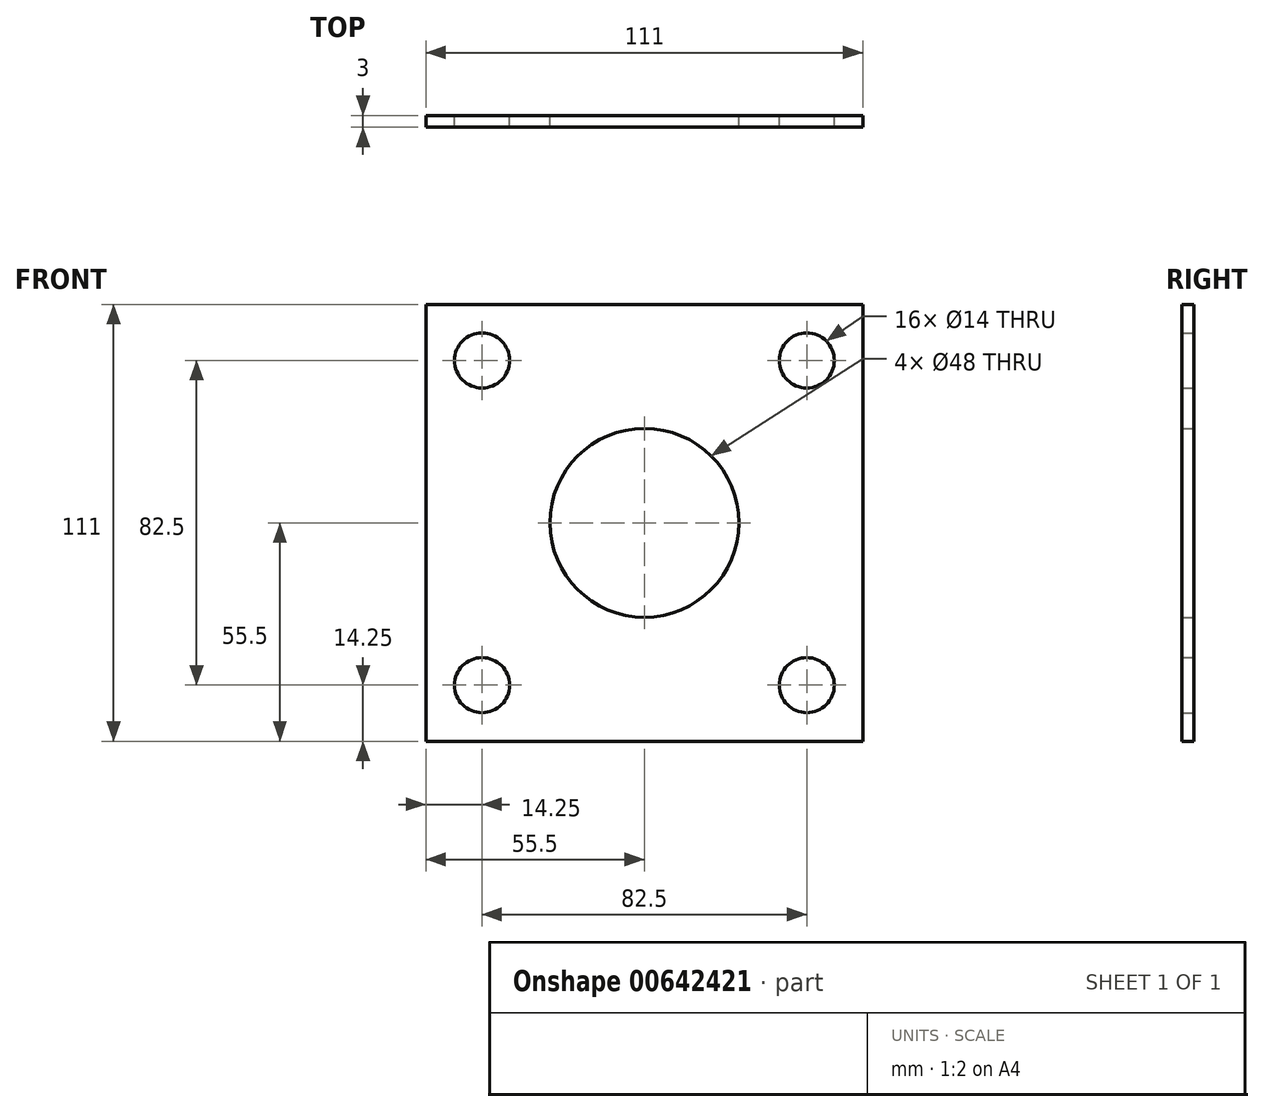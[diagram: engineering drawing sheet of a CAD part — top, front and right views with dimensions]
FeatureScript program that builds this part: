
annotation { "Feature Type Name" : "Feature", "Feature Type Description" : "" }
export const myFeature = defineFeature(function(context is Context, id is Id, definition is map)
    precondition{}
    {
        {
            var Q0;
            Q0=qCreatedBy(makeId("Front.planeOp"),FACE);
            var sketch = newSketch(context, id + "F0", { "sketchPlane" : qUnion([Q0])});
            skLineSegment(sketch, "E0.bottom", {"start": v(55.5, -55.5) * mm, "end": v(-55.5, -55.5) * mm});
            skLineSegment(sketch, "E0.top", {"start": v(55.5, 55.5) * mm, "end": v(-55.5, 55.5) * mm});
            skLineSegment(sketch, "E0.left", {"start": v(55.5, -55.5) * mm, "end": v(55.5, 55.5) * mm});
            skLineSegment(sketch, "E0.right", {"start": v(-55.5, -55.5) * mm, "end": v(-55.5, 55.5) * mm});
            skPoint(sketch, "E0.middle", {"position": v(0, 0) * mm});
            skCircle(sketch, "E1", {"center": v(-41.25, 41.25) * mm, "radius": 7 * mm});
            skCircle(sketch, "E2", {"center": v(41.25, 41.25) * mm, "radius": 7 * mm});
            skCircle(sketch, "E3", {"center": v(0, 0) * mm, "radius": 24 * mm});
            skCircle(sketch, "E4.MirrorC", {"center": v(-41.25, -41.25) * mm, "radius": 7 * mm});
            skCircle(sketch, "E5.MirrorC", {"center": v(41.25, -41.25) * mm, "radius": 7 * mm});
            skSolve(sketch);
        }
        {
            var Q0;
            Q0=makeQuery(id+"F0.imprint","IMPRINT",FACE,{"disambiguationData":[TD([[makeQuery(id+"F0.imprint","IMPRINT",EDGE,{"derivedFrom":sQuery(id+"F0.wireOp",EDGE,"E0.bottom")}),-1.0]])]});
            extrude(context, id + "F1", {"entities" : qUnion([Q0]), "depth" : 3 * mm, "offsetDistance" : 25 * mm});
        }
    });
